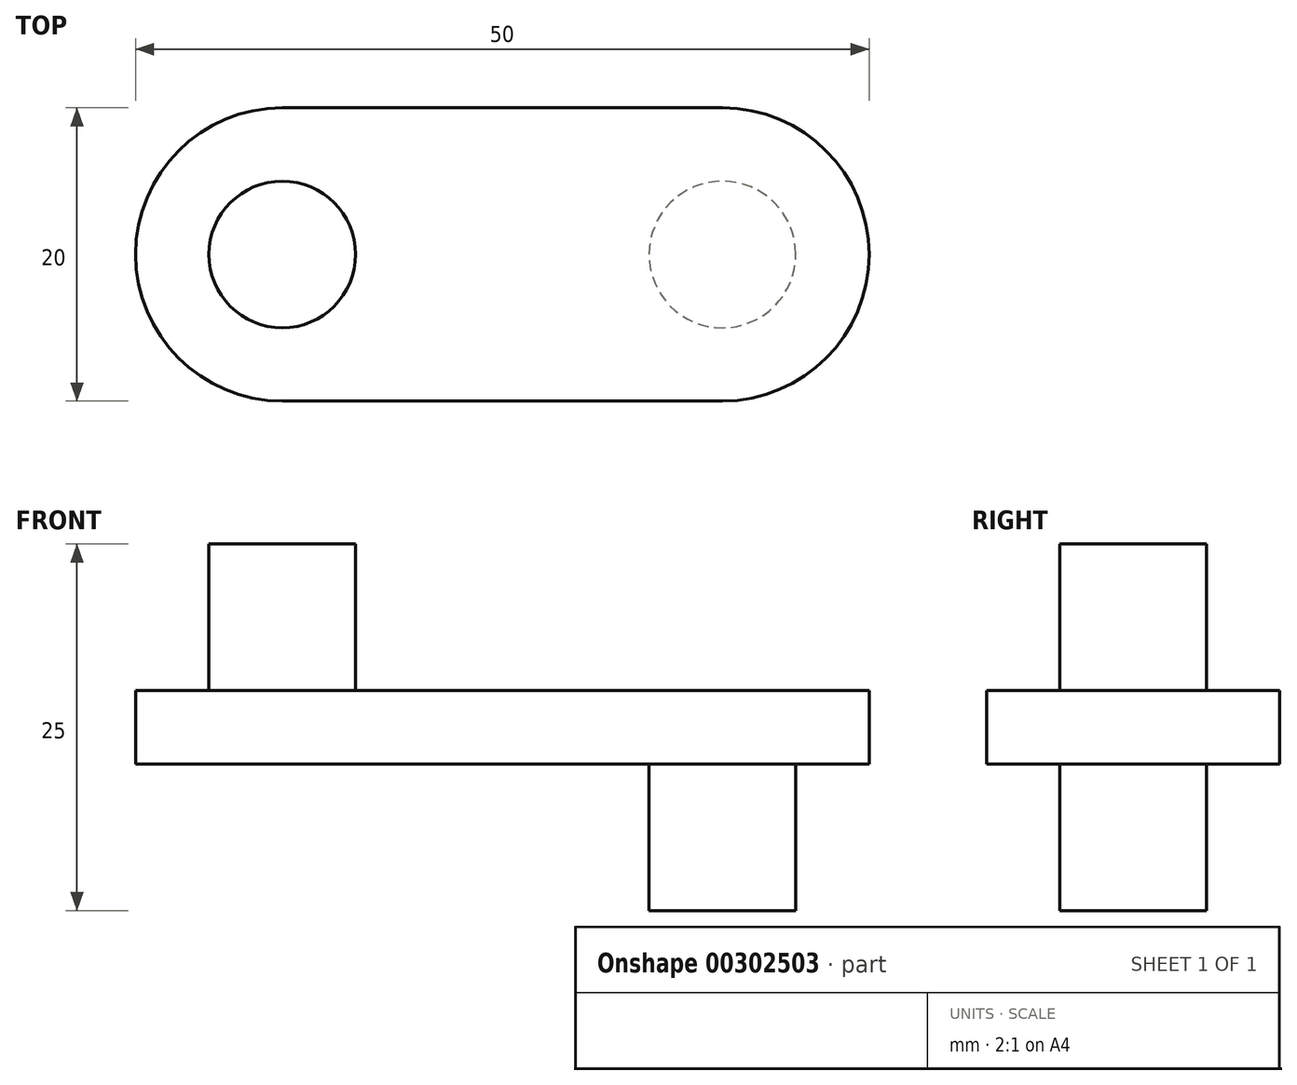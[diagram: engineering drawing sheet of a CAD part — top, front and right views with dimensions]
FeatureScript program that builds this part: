
annotation { "Feature Type Name" : "Feature", "Feature Type Description" : "" }
export const myFeature = defineFeature(function(context is Context, id is Id, definition is map)
    precondition{}
    {
        {
            var Q0;
            Q0=qCreatedBy(makeId("Top.planeOp"),FACE);
            var sketch = newSketch(context, id + "F0", { "sketchPlane" : qUnion([Q0])});
            skLineSegment(sketch, "E0", {"start": v(0, 0) * mm, "end": v(33.24, 0) * mm, "construction": true});
            skLineSegment(sketch, "E1", {"start": v(0, 0) * mm, "end": v(0, 0) * mm});
            skLineSegment(sketch, "E2", {"start": v(10, 10) * mm, "end": v(40, 10) * mm});
            skLineSegment(sketch, "E3", {"start": v(50, 0) * mm, "end": v(50, 0) * mm});
            skPoint(sketch, "E4.visualSharp", {"position": v(0, 10) * mm});
            skArc(sketch, "E4.filletArc", {"start": v(10, 10) * mm, "mid": v(2.93, 7.07) * mm, "end": v(0, 0) * mm});
            skPoint(sketch, "E5.visualSharp", {"position": v(50, 10) * mm});
            skArc(sketch, "E5.filletArc", {"start": v(50, 0) * mm, "mid": v(47.07, 7.07) * mm, "end": v(40, 10) * mm});
            skLineSegment(sketch, "E6.MirrorCS", {"start": v(10, -10) * mm, "end": v(40, -10) * mm});
            skArc(sketch, "E7.MirrorCS", {"start": v(50, 0) * mm, "mid": v(47.07, -7.07) * mm, "end": v(40, -10) * mm});
            skPoint(sketch, "E8.MirrorP", {"position": v(50, -10) * mm});
            skPoint(sketch, "E9.MirrorP", {"position": v(0, -10) * mm});
            skArc(sketch, "E10.MirrorCS", {"start": v(10, -10) * mm, "mid": v(2.93, -7.07) * mm, "end": v(0, 0) * mm});
            skCircle(sketch, "E11", {"center": v(10, 0) * mm, "radius": 5 * mm});
            skCircle(sketch, "E12", {"center": v(40, 0) * mm, "radius": 5 * mm});
            skSolve(sketch);
        }
        {
            var Q0;
            Q0=makeQuery(id+"F0.imprint","IMPRINT",FACE,{"disambiguationData":[TD([[makeQuery(id+"F0.imprint","IMPRINT",EDGE,{"derivedFrom":sQuery(id+"F0.wireOp",EDGE,"E2")}),-1.0]])]});
            var Q1;
            Q1=makeQuery(id+"F0.imprint","IMPRINT",FACE,{"disambiguationData":[TD([[makeQuery(id+"F0.imprint","IMPRINT",EDGE,{"derivedFrom":sQuery(id+"F0.wireOp",EDGE,"E11")}),1.0]])]});
            var Q2;
            Q2=makeQuery(id+"F0.imprint","IMPRINT",FACE,{"disambiguationData":[TD([[makeQuery(id+"F0.imprint","IMPRINT",EDGE,{"derivedFrom":sQuery(id+"F0.wireOp",EDGE,"E12")}),1.0]])]});
            extrude(context, id + "F1", {"entities" : qUnion([Q0, Q1, Q2]), "depth" : 5 * mm});
        }
        {
            var Q0;
            Q0=makeQuery(id+"F0.imprint","IMPRINT",FACE,{"disambiguationData":[TD([[makeQuery(id+"F0.imprint","IMPRINT",EDGE,{"derivedFrom":sQuery(id+"F0.wireOp",EDGE,"E12")}),1.0]])]});
            extrude(context, id + "F2", {"entities" : qUnion([Q0]), "operationType" : NewBodyOperationType.ADD, "oppositeDirection" : true, "depth" : 10 * mm});
        }
        {
            var Q0;
            Q0=makeQuery(id+"F0.imprint","IMPRINT",FACE,{"disambiguationData":[TD([[makeQuery(id+"F0.imprint","IMPRINT",EDGE,{"derivedFrom":sQuery(id+"F0.wireOp",EDGE,"E11")}),1.0]])]});
            extrude(context, id + "F3", {"entities" : qUnion([Q0]), "operationType" : NewBodyOperationType.ADD, "depth" : 15 * mm});
        }
    });
